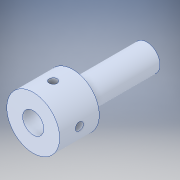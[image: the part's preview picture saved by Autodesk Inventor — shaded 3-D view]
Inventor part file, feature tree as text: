
AUTODESK INVENTOR PART (.ipt)
format: ipt  version: 2018 (Build 220112000, 112)  size: 216,576 bytes
history: native  units: in
note: dims shown in document units (in); Inventor stores cm internally (conversion verified against a paired STEP export)
features: projected_geometry x4, extrude x3, sketch x3, other x1, boolean_combine x1, pattern_circular x1
ambient origin geometry x8: Origin, YZ Plane, XZ Plane, XY Plane, X Axis, Y Axis, Z Axis, Center Point
bodies: Solid1 (feature_tree), Solid2 (feature_tree)
feature tree (13):
  other  "Cut-Extrude2"
  extrude  "Extrusion1"  Depth=0.3937in
  boolean_combine  "Combine1"
  extrude  "Extrusion2"  Depth=0.7874in TaperAngle=0.0deg
  extrude  "Extrusion3"  [1 undecoded]
  sketch  "Sketch1"  dims[d0=0.315in d1=0.3937in]
  sketch  "Sketch2"  dims[d2=0.0in d3=0.0in d4=0.7874in d5=0.0in]
  projected_geometry  "Projected Loop1"
  sketch  "Sketch3"  dims[d6=0.7874in d7=0.0in]
  projected_geometry  "Projected Loop2"
  projected_geometry  "Projected Loop3"
  pattern_circular  "CirPattern1"
  projected_geometry  "Project Cut Edges1"
note: 1 required parameter value undecoded (feature->parameter linkage not recoverable at this tier; creation-order binding heuristic only, values carry confidence <= 0.55)
